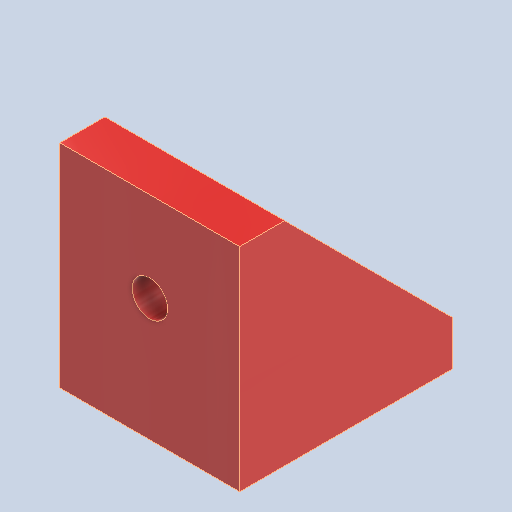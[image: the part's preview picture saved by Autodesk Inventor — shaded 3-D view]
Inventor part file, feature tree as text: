
AUTODESK INVENTOR PART (.ipt)
format: ipt  version: 2023 (Build 270158000, 158)  size: 152,064 bytes
history: native  units: in
note: dims shown in document units (in); Inventor stores cm internally (conversion verified against a paired STEP export)
features: extrude x5, sketch x5, chamfer x3, projected_geometry x2
ambient origin geometry x8: Origin, YZ Plane, XZ Plane, XY Plane, X Axis, Y Axis, Z Axis, Center Point
bodies: Solid1 (feature_tree)
feature tree (15):
  extrude  "Extrusion1"  Depth=1.1811in
  extrude  "Extrusion2"  Depth=0.25in
  extrude  "Extrusion3"  Depth=1.0in
  extrude  "Extrusion4"  Depth=0.5in
  extrude  "Extrusion5"  Depth=0.125in
  chamfer  "Chamfer1"  Distance=0.5in
  chamfer  "Chamfer2"  Distance=0.5in
  chamfer  "Chamfer3"  [1 undecoded]
  sketch  "Sketch1"  dims[d0=1.1811in d1=1.1811in]
  sketch  "Sketch2"  dims[d2=0.25in d3=0.25in]
  sketch  "Sketch3"  dims[d4=1.0in d5=0.0in d6=0.1969in]
  sketch  "Sketch4"  dims[d7=0.5in d8=0.5in]
  projected_geometry  "Projected Loop1"
  sketch  "Sketch5"  dims[d9=0.0in d10=0.0in d11=0.1969in d12=0.5in d13=0.5in d14=0.0in d15=0.0in d16=0.125in d17=1.0in d18=0.0in d19=1.0in d20=0.0in d21=0.1939in d22=0.125in d23=45.0deg d24=0.193in d25=0.125in d26=45.0deg d27=0.193in d28=0.125in d29=45.0deg]
  projected_geometry  "Projected Loop2"
note: 1 required parameter value undecoded (feature->parameter linkage not recoverable at this tier; creation-order binding heuristic only, values carry confidence <= 0.55)
